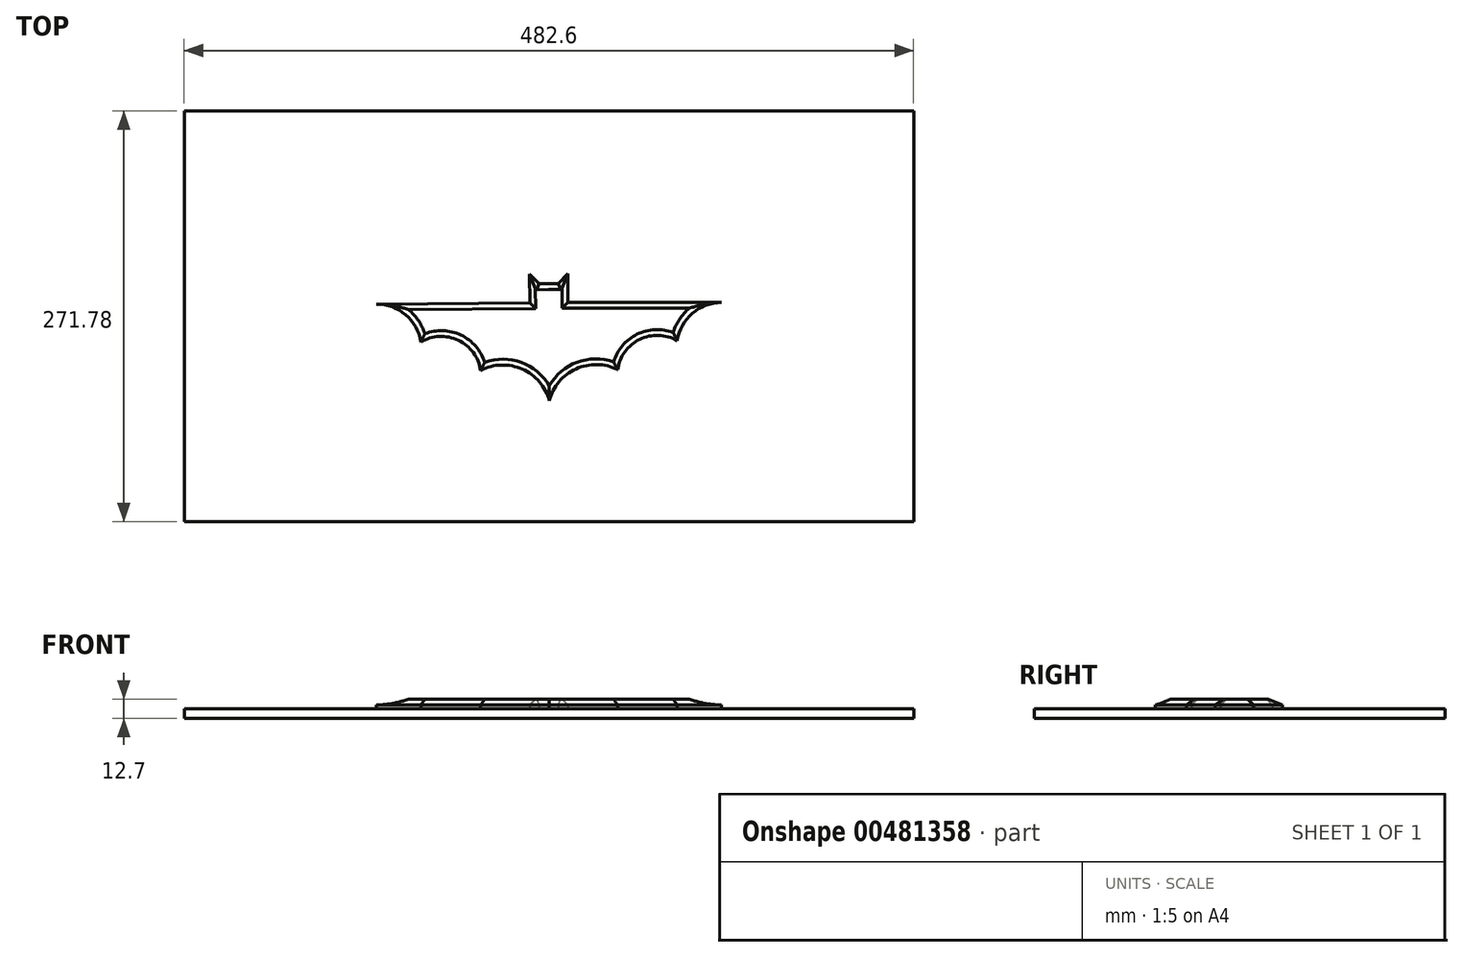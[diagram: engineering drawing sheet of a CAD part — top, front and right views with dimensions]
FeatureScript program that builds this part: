
annotation { "Feature Type Name" : "Feature", "Feature Type Description" : "" }
export const myFeature = defineFeature(function(context is Context, id is Id, definition is map)
    precondition{}
    {
        {
            var Q0;
            Q0=qCreatedBy(makeId("Top.planeOp"),FACE);
            var sketch = newSketch(context, id + "F0", { "sketchPlane" : qUnion([Q0])});
            skLineSegment(sketch, "E0", {"start": v(-89.28, 9.07) * mm, "end": v(-13.08, 9.07) * mm});
            skLineSegment(sketch, "E1", {"start": v(-13.08, 9.07) * mm, "end": v(-13.08, 28.12) * mm});
            skLineSegment(sketch, "E2", {"start": v(-13.08, 28.12) * mm, "end": v(-6.73, 21.45) * mm});
            skLineSegment(sketch, "E3", {"start": v(-6.73, 21.45) * mm, "end": v(5.97, 21.45) * mm});
            skLineSegment(sketch, "E4", {"start": v(5.97, 21.45) * mm, "end": v(12.32, 28.12) * mm});
            skLineSegment(sketch, "E5", {"start": v(12.32, 28.12) * mm, "end": v(12.32, 9.07) * mm});
            skLineSegment(sketch, "E6", {"start": v(12.32, 9.07) * mm, "end": v(113.92, 9.07) * mm});
            skLineSegment(sketch, "E7", {"start": v(-0.38, 21.45) * mm, "end": v(0, -55.89) * mm});
            skArc(sketch, "E8", {"start": v(45.2, -35.36) * mm, "mid": v(17.7, -34.82) * mm, "end": v(0, -55.89) * mm});
            skArc(sketch, "E9", {"start": v(84.59, -16.23) * mm, "mid": v(59.8, -15.3) * mm, "end": v(45.2, -35.36) * mm});
            skArc(sketch, "E10", {"start": v(113.92, 9.07) * mm, "mid": v(94.55, 1.87) * mm, "end": v(84.59, -16.23) * mm});
            skSolve(sketch);
        }
        {
            var Q0;
            {var subQ0=sQuery(id+"F0.wireOp",EDGE,"E4");Q0=makeQuery(id+"F0.imprint","IMPRINT",FACE,{"disambiguationData":[TD([[makeQuery(id+"F0.imprint","IMPRINT",EDGE,{"derivedFrom":subQ0}),-1.0]])]});}
            extrude(context, id + "F1", {"entities" : qUnion([Q0]), "depth" : 6.35 * mm});
        }
        {
            var Q0;
            Q0=makeQuery(id+"F1.opExtrude","SWEPT_BODY",BODY,{"disambiguationData":[OSD([sQuery(id+"F0.wireOp",EDGE,"E3"),sQuery(id+"F0.wireOp",EDGE,"E4"),sQuery(id+"F0.wireOp",EDGE,"E5"),sQuery(id+"F0.wireOp",EDGE,"E6"),sQuery(id+"F0.wireOp",EDGE,"E7"),sQuery(id+"F0.wireOp",EDGE,"E8"),sQuery(id+"F0.wireOp",EDGE,"E9"),sQuery(id+"F0.wireOp",EDGE,"E10")])]});
            var Q1;
            Q1=makeQuery(id+"F1.opExtrude","SWEPT_FACE",FACE,{"disambiguationData":[OSD([sQuery(id+"F0.wireOp",EDGE,"E7")])]});
            mirror(context, id + "F2", {"operationType" : NewBodyOperationType.ADD, "entities" : qUnion([Q0]), "mirrorPlane" : qUnion([Q1])});
        }
        {
            var Q0;
            {var subQ0=makeQuery(id+"F1.opExtrude","CAP_FACE",FACE,{"disambiguationData":[OSD([sQuery(id+"F0.wireOp",EDGE,"E3"),sQuery(id+"F0.wireOp",EDGE,"E4"),sQuery(id+"F0.wireOp",EDGE,"E5"),sQuery(id+"F0.wireOp",EDGE,"E6"),sQuery(id+"F0.wireOp",EDGE,"E7"),sQuery(id+"F0.wireOp",EDGE,"E8"),sQuery(id+"F0.wireOp",EDGE,"E9"),sQuery(id+"F0.wireOp",EDGE,"E10")])],"isStart":false});Q0=makeQuery(id+"F2.boolean.opBoolean","MERGE",FACE,{"derivedFrom":[subQ0,makeQuery(id+"F2.opPattern","COPY",FACE,{"derivedFrom":subQ0,"instanceName":"1"})]});}
            chamfer(context, id + "F3", {"entities" : qUnion([Q0]), "width" : 3.8 * mm, "tangentPropagation" : true});
        }
        {
            var Q0;
            Q0=qCreatedBy(makeId("Top.planeOp"),FACE);
            cPlane(context, id + "F4", {"entities" : qUnion([Q0]), "cplaneType" : CPlaneType.OFFSET, "offset" : 6.35 * mm, "oppositeDirection" : true, "width" : 152.4 * mm, "height" : 152.4 * mm});
        }
        {
            var Q0;
            Q0=qCreatedBy(id+"F4.planeOp",FACE);
            var sketch = newSketch(context, id + "F5", { "sketchPlane" : qUnion([Q0])});
            skLineSegment(sketch, "E11.bottom", {"start": v(-241.59, -135.9) * mm, "end": v(241.01, -135.9) * mm});
            skLineSegment(sketch, "E11.top", {"start": v(-241.59, 135.89) * mm, "end": v(241.01, 135.89) * mm});
            skLineSegment(sketch, "E11.left", {"start": v(-241.59, -135.9) * mm, "end": v(-241.59, 135.89) * mm});
            skLineSegment(sketch, "E11.right", {"start": v(241.01, -135.9) * mm, "end": v(241.01, 135.89) * mm});
            skSolve(sketch);
        }
        {
            var Q0;
            Q0 = qSketchRegion(id + "F5", true);
            extrude(context, id + "F6", {"entities" : qUnion([Q0]), "depth" : 6.35 * mm});
        }
    });
